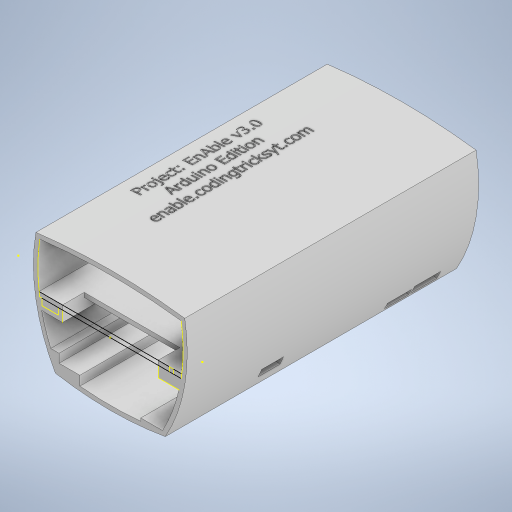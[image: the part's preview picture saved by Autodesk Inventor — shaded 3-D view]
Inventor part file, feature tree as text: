
AUTODESK INVENTOR PART (.ipt)
format: ipt  version: 2024 (Build 280153000, 153)  size: 1,962,496 bytes
history: native  units: in
note: dims shown in document units (in); Inventor stores cm internally (conversion verified against a paired STEP export)
features: extrude x13, sketch x6, plane x5
ambient origin geometry x8: Origin, YZ Plane, XZ Plane, XY Plane, X Axis, Y Axis, Z Axis, Center Point
bodies: Body1 (feature_tree)
feature tree (24):
  sketch  "Sketch1"  dims[d19=2.5591in d20=0.9055in]
  extrude  "Extrusion3"  Depth=0.9055in
  extrude  "Extrusion4"  Depth=1.8898in
  plane  "Work Plane2"
  plane  "Work Plane4"
  extrude  "Extrusion7"  Depth=0.3346in
  extrude  "Extrusion8"  Depth=0.0787in
  extrude  "Extrusion9"  Depth=0.0787in
  plane  "Work Plane5"
  extrude  "Extrusion10"  Depth=0.1969in
  plane  "Work Plane6"
  extrude  "Extrusion11"  Depth=0.3937in
  extrude  "Extrusion12"  Depth=0.3937in
  sketch  "Sketch11"  dims[d40=0.9843in d41=0.3346in]
  extrude  "Extrusion15"  Depth=0.3937in
  plane  "Work Plane7"
  extrude  "Extrusion18"  Depth=0.0787in
  extrude  "Extrusion19"  Depth=0.0787in
  extrude  "Extrusion17"  Depth=0.3937in TaperAngle=0.0deg
  extrude  "Extrusion20"  Depth=0.0787in TaperAngle=0.0deg
  sketch  "Sketch8"  dims[d30=2.5591in d39=1.8898in]
  sketch  "Sketch12"  dims[d42=0.3346in d43=0.0787in]
  sketch  "Sketch14"  dims[d44=0.0787in d45=2.126in]
  sketch  "Sketch15"  dims[d46=0.1969in d47=0.1969in d48=0.3937in d49=0.3937in d54=0.1181in d55=0.0787in d56=0.0787in d57=3.937in d58=0.0in d59=0.0787in d60=0.0in d68=0.1181in d69=0.0787in d70=0.0787in d76=0.315in d77=0.1575in d78=0.4724in d79=0.0394in d80=0.1181in d81=0.4331in d82=0.3937in d83=0.0in d84=0.0787in d85=0.1575in d86=0.3937in d87=0.0in d88=0.0787in d89=0.3937in d90=0.0in d91=3.2283in d92=0.315in d93=0.3937in d94=0.1575in d95=3.2283in d96=0.1575in d97=0.3937in d98=0.3937in d99=0.0in d100=1.2598in d101=0.0in d102=1.2598in d104=0.1181in d106=0.1181in d107=1.2598in d108=0.0in d121=0.3937in d122=0.3937in d123=0.9055in d124=0.9843in d125=1.2795in d126=0.0787in d127=0.0787in d128=0.313in d129=0.5467in d130=0.8983in d131=0.6979in d134=0.3937in d135=0.0in d138=1.0512in d139=1.0512in d140=1.2992in d141=90.0deg d142=1.2992in d143=2.5984in d144=0.0787in d146=1.4961in d148=0.1181in d150=0.1181in d151=0.5433in d152=0.1181in d153=0.5906in d154=0.1181in d155=0.3937in d156=0.0in d157=0.0689in d158=0.0in d159=0.3937in d160=0.0in d161=0.3937in d162=0.0in d103=0.0344in]
